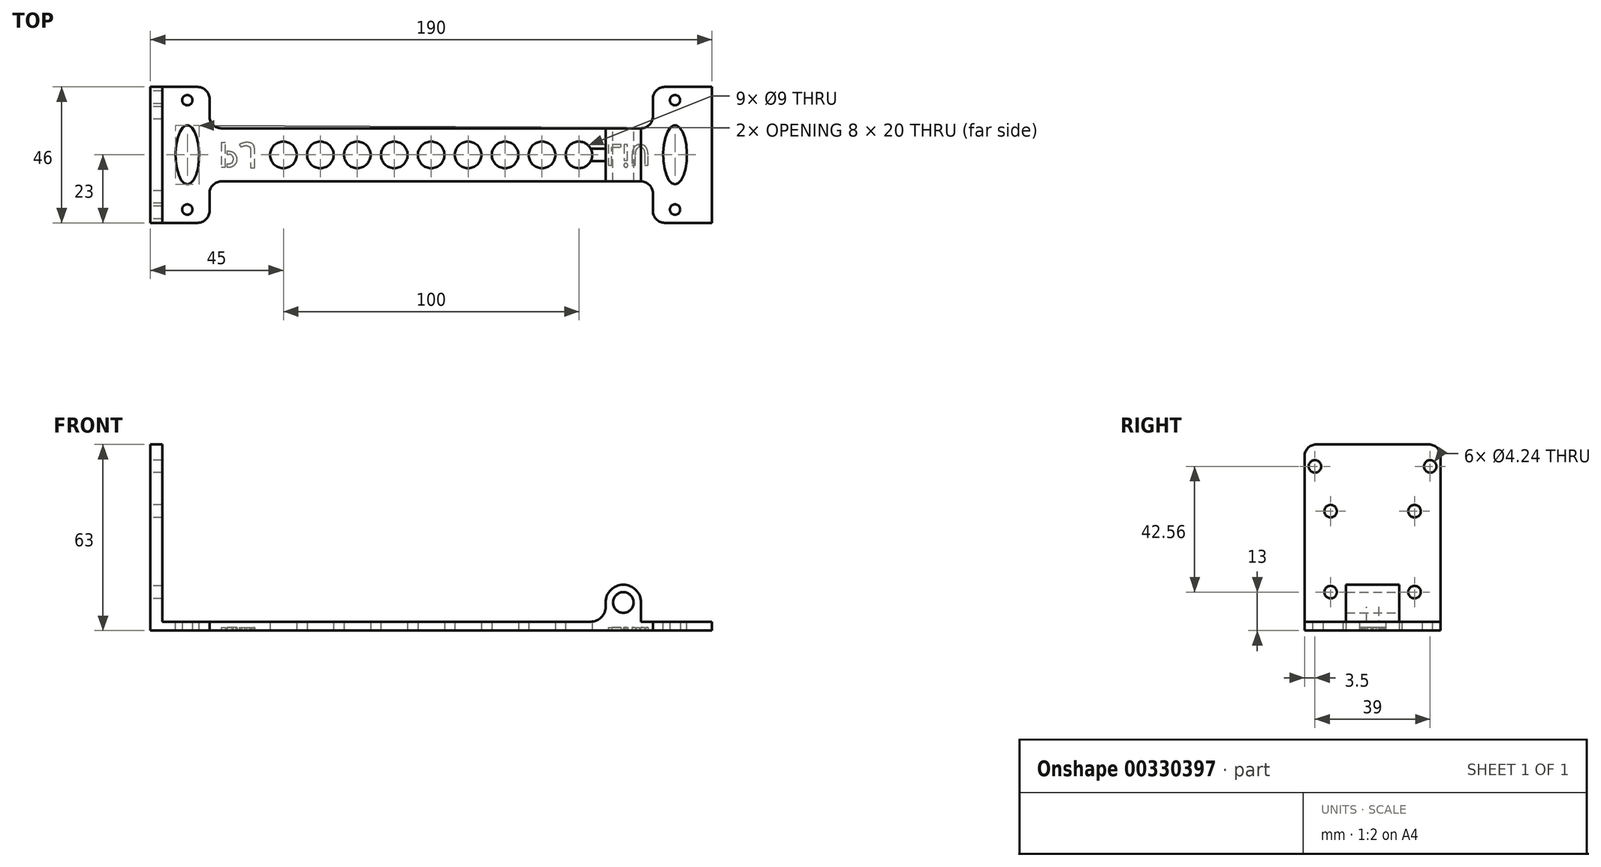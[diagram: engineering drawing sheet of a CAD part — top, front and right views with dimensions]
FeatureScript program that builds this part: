
annotation { "Feature Type Name" : "Feature", "Feature Type Description" : "" }
export const myFeature = defineFeature(function(context is Context, id is Id, definition is map)
    precondition{}
    {
        {
            var Q0;
            Q0=qCreatedBy(makeId("Top.planeOp"),FACE);
            var sketch = newSketch(context, id + "F0", { "sketchPlane" : qUnion([Q0])});
            skLineSegment(sketch, "E0.bottom", {"start": v(-75, 9) * mm, "end": v(75, 9) * mm});
            skLineSegment(sketch, "E0.top", {"start": v(-75, -9) * mm, "end": v(75, -9) * mm});
            skLineSegment(sketch, "E0.left", {"start": v(-75, 9) * mm, "end": v(-75, -9) * mm});
            skLineSegment(sketch, "E0.right", {"start": v(75, 9) * mm, "end": v(75, -9) * mm});
            skPoint(sketch, "E0.middle", {"position": v(0, 0) * mm});
            skLineSegment(sketch, "E1", {"start": v(-95, 23) * mm, "end": v(-95, -23) * mm});
            skPoint(sketch, "E2.middle.positionSnap0", {"position": v(0, 9) * mm});
            skPoint(sketch, "E2.centerSnap0", {"position": v(0, 9) * mm});
            skCircle(sketch, "E3", {"center": v(-82.5, 18.5) * mm, "radius": 1.75 * mm});
            skCircle(sketch, "E4.MirrorC", {"center": v(-82.5, -18.5) * mm, "radius": 1.75 * mm});
            skLineSegment(sketch, "E5", {"start": v(-95, 23) * mm, "end": v(-75, 23) * mm});
            skLineSegment(sketch, "E6", {"start": v(-75, 9) * mm, "end": v(-75, 23) * mm});
            skLineSegment(sketch, "E7.MirrorCS", {"start": v(-95, -23) * mm, "end": v(-75, -23) * mm});
            skLineSegment(sketch, "E8.MirrorCS", {"start": v(-75, -9) * mm, "end": v(-75, -23) * mm});
            skLineSegment(sketch, "E9.MirrorCS", {"start": v(95, 23) * mm, "end": v(95, -23) * mm});
            skLineSegment(sketch, "E10.MirrorCS", {"start": v(95, -23) * mm, "end": v(75, -23) * mm});
            skCircle(sketch, "E11.MirrorC", {"center": v(82.5, -18.5) * mm, "radius": 1.75 * mm});
            skCircle(sketch, "E12.MirrorC", {"center": v(82.5, 18.5) * mm, "radius": 1.75 * mm});
            skLineSegment(sketch, "E13.MirrorCS", {"start": v(95, 23) * mm, "end": v(75, 23) * mm});
            skLineSegment(sketch, "E14.MirrorCS", {"start": v(75, 9) * mm, "end": v(75, 23) * mm});
            skLineSegment(sketch, "E15.MirrorCS", {"start": v(75, -9) * mm, "end": v(75, -23) * mm});
            skSolve(sketch);
        }
        {
            var Q0;
            Q0=makeQuery(id+"F0.imprint","IMPRINT",FACE,{"disambiguationData":[TD([[makeQuery(id+"F0.imprint","IMPRINT",EDGE,{"derivedFrom":sQuery(id+"F0.wireOp",EDGE,"E0.bottom")}),-1.0]])]});
            var Q1;
            Q1=makeQuery(id+"F0.imprint","IMPRINT",FACE,{"disambiguationData":[TD([[makeQuery(id+"F0.imprint","IMPRINT",EDGE,{"derivedFrom":sQuery(id+"F0.wireOp",EDGE,"E0.left")}),-1.0]])]});
            var Q2;
            Q2=makeQuery(id+"F0.imprint","IMPRINT",FACE,{"disambiguationData":[TD([[makeQuery(id+"F0.imprint","IMPRINT",EDGE,{"derivedFrom":sQuery(id+"F0.wireOp",EDGE,"E0.right")}),1.0]])]});
            extrude(context, id + "F1", {"entities" : qUnion([Q0, Q1, Q2]), "endBound" : BoundingType.SYMMETRIC, "depth" : 3 * mm});
        }
        {
            var Q0;
            Q0=makeQuery(id+"F1.opExtrude","SWEPT_FACE",FACE,{"disambiguationData":[OSD([sQuery(id+"F0.wireOp",EDGE,"E0.bottom")])]});
            var sketch = newSketch(context, id + "F2", { "sketchPlane" : qUnion([Q0])});
            skCircle(sketch, "E16", {"center": v(-65, 8) * mm, "radius": 3.5 * mm});
            skArc(sketch, "E17", {"start": v(-59, 8) * mm, "mid": v(-65, 14) * mm, "end": v(-71, 8) * mm});
            skLineSegment(sketch, "E18", {"start": v(-59, 8) * mm, "end": v(-59, 1.5) * mm});
            skLineSegment(sketch, "E19", {"start": v(-71, 1.5) * mm, "end": v(-71, 8) * mm});
            skArc(sketch, "E20.MirrorCS", {"start": v(59, 8) * mm, "mid": v(65, 14) * mm, "end": v(71, 8) * mm});
            skLineSegment(sketch, "E21.MirrorCS", {"start": v(59, 8) * mm, "end": v(59, 1.5) * mm});
            skLineSegment(sketch, "E22.MirrorCS", {"start": v(71, 1.5) * mm, "end": v(71, 8) * mm});
            skCircle(sketch, "E23.MirrorC", {"center": v(65, 8) * mm, "radius": 3.5 * mm});
            skSolve(sketch);
        }
        {
            var Q0;
            Q0=makeQuery(id+"F2.imprint","IMPRINT",FACE,{"disambiguationData":[TD([[makeQuery(id+"F2.imprint","IMPRINT",EDGE,{"derivedFrom":sQuery(id+"F2.wireOp",EDGE,"E16")}),-1.0]])]});
            var Q1;
            Q1=makeQuery(id+"F2.imprint","IMPRINT",FACE,{"disambiguationData":[TD([[makeQuery(id+"F2.imprint","IMPRINT",EDGE,{"derivedFrom":sQuery(id+"F2.wireOp",EDGE,"E20.MirrorCS")}),-1.0]])]});
            extrude(context, id + "F3", {"entities" : qUnion([Q0, Q1]), "operationType" : NewBodyOperationType.ADD, "oppositeDirection" : true, "depth" : 18 * mm});
        }
        {
            var Q0;
            Q0=makeQuery(id+"F1.opExtrude","CAP_FACE",FACE,{"disambiguationData":[OSD([sQuery(id+"F0.wireOp",EDGE,"E0.bottom"),sQuery(id+"F0.wireOp",EDGE,"E0.top"),sQuery(id+"F0.wireOp",EDGE,"E1"),sQuery(id+"F0.wireOp",EDGE,"E3"),sQuery(id+"F0.wireOp",EDGE,"E4.MirrorC"),sQuery(id+"F0.wireOp",EDGE,"E5"),sQuery(id+"F0.wireOp",EDGE,"E6"),sQuery(id+"F0.wireOp",EDGE,"E7.MirrorCS"),sQuery(id+"F0.wireOp",EDGE,"E8.MirrorCS"),sQuery(id+"F0.wireOp",EDGE,"E9.MirrorCS"),sQuery(id+"F0.wireOp",EDGE,"E10.MirrorCS"),sQuery(id+"F0.wireOp",EDGE,"E11.MirrorC"),sQuery(id+"F0.wireOp",EDGE,"E12.MirrorC"),sQuery(id+"F0.wireOp",EDGE,"E13.MirrorCS"),sQuery(id+"F0.wireOp",EDGE,"E14.MirrorCS"),sQuery(id+"F0.wireOp",EDGE,"E15.MirrorCS")])],"isStart":true});
            var sketch = newSketch(context, id + "F4", { "sketchPlane" : qUnion([Q0])});
            skCircle(sketch, "E24", {"center": v(-50, 0) * mm, "radius": 4.5 * mm});
            skCircle(sketch, "E25.1.0.0", {"center": v(-37.5, 0) * mm, "radius": 4.5 * mm});
            skCircle(sketch, "E25.2.0.0", {"center": v(-25, 0) * mm, "radius": 4.5 * mm});
            skCircle(sketch, "E25.3.0.0", {"center": v(-12.5, 0) * mm, "radius": 4.5 * mm});
            skCircle(sketch, "E25.4.0.0", {"center": v(0, 0) * mm, "radius": 4.5 * mm});
            skCircle(sketch, "E25.5.0.0", {"center": v(12.5, 0) * mm, "radius": 4.5 * mm});
            skCircle(sketch, "E25.6.0.0", {"center": v(25, 0) * mm, "radius": 4.5 * mm});
            skCircle(sketch, "E25.7.0.0", {"center": v(37.5, 0) * mm, "radius": 4.5 * mm});
            skCircle(sketch, "E25.8.0.0", {"center": v(50, 0) * mm, "radius": 4.5 * mm});
            skLineSegment(sketch, "E25.direction1", {"start": v(-50, 0) * mm, "end": v(-37.5, 0) * mm, "construction": true});
            skEllipse(sketch, "E26", {"center": v(-82.5, 0) * mm, "majorRadius": 10 * mm, "minorRadius": 4 * mm, "majorAxis": v(0, 1)});
            skEllipse(sketch, "E27.MirrorC", {"center": v(82.5, 0) * mm, "majorRadius": 10 * mm, "minorRadius": 4 * mm, "majorAxis": v(0, 1)});
            skSolve(sketch);
        }
        {
            var Q0;
            Q0=makeQuery(id+"F4.imprint","IMPRINT",FACE,{"disambiguationData":[TD([[makeQuery(id+"F4.imprint","IMPRINT",EDGE,{"derivedFrom":sQuery(id+"F4.wireOp",EDGE,"E24")}),1.0]])]});
            var Q1;
            Q1=makeQuery(id+"F4.imprint","IMPRINT",FACE,{"disambiguationData":[TD([[makeQuery(id+"F4.imprint","IMPRINT",EDGE,{"derivedFrom":sQuery(id+"F4.wireOp",EDGE,"E25.1.0.0")}),1.0]])]});
            var Q2;
            Q2=makeQuery(id+"F4.imprint","IMPRINT",FACE,{"disambiguationData":[TD([[makeQuery(id+"F4.imprint","IMPRINT",EDGE,{"derivedFrom":sQuery(id+"F4.wireOp",EDGE,"E25.2.0.0")}),1.0]])]});
            var Q3;
            Q3=makeQuery(id+"F4.imprint","IMPRINT",FACE,{"disambiguationData":[TD([[makeQuery(id+"F4.imprint","IMPRINT",EDGE,{"derivedFrom":sQuery(id+"F4.wireOp",EDGE,"E25.3.0.0")}),1.0]])]});
            var Q4;
            Q4=makeQuery(id+"F4.imprint","IMPRINT",FACE,{"disambiguationData":[TD([[makeQuery(id+"F4.imprint","IMPRINT",EDGE,{"derivedFrom":sQuery(id+"F4.wireOp",EDGE,"E25.4.0.0")}),1.0]])]});
            var Q5;
            Q5=makeQuery(id+"F4.imprint","IMPRINT",FACE,{"disambiguationData":[TD([[makeQuery(id+"F4.imprint","IMPRINT",EDGE,{"derivedFrom":sQuery(id+"F4.wireOp",EDGE,"E25.5.0.0")}),1.0]])]});
            var Q6;
            Q6=makeQuery(id+"F4.imprint","IMPRINT",FACE,{"disambiguationData":[TD([[makeQuery(id+"F4.imprint","IMPRINT",EDGE,{"derivedFrom":sQuery(id+"F4.wireOp",EDGE,"E25.6.0.0")}),1.0]])]});
            var Q7;
            Q7=makeQuery(id+"F4.imprint","IMPRINT",FACE,{"disambiguationData":[TD([[makeQuery(id+"F4.imprint","IMPRINT",EDGE,{"derivedFrom":sQuery(id+"F4.wireOp",EDGE,"E25.7.0.0")}),1.0]])]});
            var Q8;
            Q8=makeQuery(id+"F4.imprint","IMPRINT",FACE,{"disambiguationData":[TD([[makeQuery(id+"F4.imprint","IMPRINT",EDGE,{"derivedFrom":sQuery(id+"F4.wireOp",EDGE,"E25.8.0.0")}),1.0]])]});
            var Q9;
            Q9=makeQuery(id+"F4.imprint","IMPRINT",FACE,{"disambiguationData":[TD([[makeQuery(id+"F4.imprint","IMPRINT",EDGE,{"derivedFrom":sQuery(id+"F4.wireOp",EDGE,"E26")}),1.0]])]});
            var Q10;
            Q10=makeQuery(id+"F4.imprint","IMPRINT",FACE,{"disambiguationData":[TD([[makeQuery(id+"F4.imprint","IMPRINT",EDGE,{"derivedFrom":sQuery(id+"F4.wireOp",EDGE,"E27.MirrorC")}),1.0]])]});
            extrude(context, id + "F5", {"entities" : qUnion([Q0, Q1, Q2, Q3, Q4, Q5, Q6, Q7, Q8, Q9, Q10]), "operationType" : NewBodyOperationType.REMOVE, "endBound" : BoundingType.UP_TO_NEXT, "oppositeDirection" : true, "depth" : 25 * mm});
        }
        {
            var Q0;
            Q0=makeQuery(id+"F3.opExtrude","SWEPT_EDGE",EDGE,{"disambiguationData":[OSD([sQuery(id+"F0.wireOp",EDGE,"E0.bottom"),sQuery(id+"F2.wireOp",EDGE,"E19")])]});
            var Q1;
            Q1=makeQuery(id+"F3.opExtrude","SWEPT_EDGE",EDGE,{"disambiguationData":[OSD([sQuery(id+"F0.wireOp",EDGE,"E0.bottom"),sQuery(id+"F2.wireOp",EDGE,"E18")])]});
            var Q2;
            Q2=makeQuery(id+"F3.opExtrude","SWEPT_EDGE",EDGE,{"disambiguationData":[OSD([sQuery(id+"F0.wireOp",EDGE,"E0.bottom"),sQuery(id+"F2.wireOp",EDGE,"E21.MirrorCS")])]});
            var Q3;
            Q3=makeQuery(id+"F3.opExtrude","SWEPT_EDGE",EDGE,{"disambiguationData":[OSD([sQuery(id+"F0.wireOp",EDGE,"E0.bottom"),sQuery(id+"F2.wireOp",EDGE,"E22.MirrorCS")])]});
            fillet(context, id + "F6", {"entities" : qUnion([Q0, Q1, Q2, Q3]), "radius" : 5 * mm, "tangentPropagation" : true, "allowEdgeOverflow" : false});
        }
        {
            var Q0;
            Q0=makeQuery(id+"F1.opExtrude","CAP_FACE",FACE,{"disambiguationData":[OSD([sQuery(id+"F0.wireOp",EDGE,"E0.bottom"),sQuery(id+"F0.wireOp",EDGE,"E0.top"),sQuery(id+"F0.wireOp",EDGE,"E1"),sQuery(id+"F0.wireOp",EDGE,"E3"),sQuery(id+"F0.wireOp",EDGE,"E4.MirrorC"),sQuery(id+"F0.wireOp",EDGE,"E5"),sQuery(id+"F0.wireOp",EDGE,"E6"),sQuery(id+"F0.wireOp",EDGE,"E7.MirrorCS"),sQuery(id+"F0.wireOp",EDGE,"E8.MirrorCS"),sQuery(id+"F0.wireOp",EDGE,"E9.MirrorCS"),sQuery(id+"F0.wireOp",EDGE,"E10.MirrorCS"),sQuery(id+"F0.wireOp",EDGE,"E11.MirrorC"),sQuery(id+"F0.wireOp",EDGE,"E12.MirrorC"),sQuery(id+"F0.wireOp",EDGE,"E13.MirrorCS"),sQuery(id+"F0.wireOp",EDGE,"E14.MirrorCS"),sQuery(id+"F0.wireOp",EDGE,"E15.MirrorCS")])],"isStart":true});
            var sketch = newSketch(context, id + "F7", { "sketchPlane" : qUnion([Q0])});
            skText(sketch, "E28", { "text": "PJ", "fontName": "AllertaStencil-Regular.ttf"});
            skText(sketch, "E29", { "text": "LiU", "fontName": "AllertaStencil-Regular.ttf"});
            const initialGuessF7  = {"E28": [-0.072, -0.00417, 1, 0, 0.00833], "E29": [0.059, -0.00346, 1, 0, 0.00692]};
            skSetInitialGuess(sketch, initialGuessF7);
            skSolve(sketch);
        }
        {
            var Q0;
            Q0=makeQuery(id+"F7.imprint","IMPRINT",FACE,{"disambiguationData":[TD([[makeQuery(id+"F7.imprint","IMPRINT",EDGE,{"derivedFrom":sQuery(id+"F7.wireOp",EDGE,"E28.sketch_text.stroke-4")}),-1.0]])]});
            var Q1;
            Q1=makeQuery(id+"F7.imprint","IMPRINT",FACE,{"disambiguationData":[TD([[makeQuery(id+"F7.imprint","IMPRINT",EDGE,{"derivedFrom":sQuery(id+"F7.wireOp",EDGE,"E28.sketch_text.stroke-0")}),-1.0]])]});
            var Q2;
            Q2=makeQuery(id+"F7.imprint","IMPRINT",FACE,{"disambiguationData":[TD([[makeQuery(id+"F7.imprint","IMPRINT",EDGE,{"derivedFrom":sQuery(id+"F7.wireOp",EDGE,"E28.sketch_text.stroke-26")}),-1.0]])]});
            var Q3;
            Q3=makeQuery(id+"F7.imprint","IMPRINT",FACE,{"disambiguationData":[TD([[makeQuery(id+"F7.imprint","IMPRINT",EDGE,{"derivedFrom":sQuery(id+"F7.wireOp",EDGE,"E29.sketch_text.stroke-0")}),-1.0]])]});
            var Q4;
            Q4=makeQuery(id+"F7.imprint","IMPRINT",FACE,{"disambiguationData":[TD([[makeQuery(id+"F7.imprint","IMPRINT",EDGE,{"derivedFrom":sQuery(id+"F7.wireOp",EDGE,"E29.sketch_text.stroke-6")}),-1.0]])]});
            var Q5;
            Q5=makeQuery(id+"F7.imprint","IMPRINT",FACE,{"disambiguationData":[TD([[makeQuery(id+"F7.imprint","IMPRINT",EDGE,{"derivedFrom":sQuery(id+"F7.wireOp",EDGE,"E29.sketch_text.stroke-10")}),-1.0]])]});
            var Q6;
            Q6=makeQuery(id+"F7.imprint","IMPRINT",FACE,{"disambiguationData":[TD([[makeQuery(id+"F7.imprint","IMPRINT",EDGE,{"derivedFrom":sQuery(id+"F7.wireOp",EDGE,"E29.sketch_text.stroke-18")}),-1.0]])]});
            var Q7;
            Q7=makeQuery(id+"F7.imprint","IMPRINT",FACE,{"disambiguationData":[TD([[makeQuery(id+"F7.imprint","IMPRINT",EDGE,{"derivedFrom":sQuery(id+"F7.wireOp",EDGE,"E29.sketch_text.stroke-30")}),-1.0]])]});
            extrude(context, id + "F8", {"entities" : qUnion([Q0, Q1, Q2, Q3, Q4, Q5, Q6, Q7]), "operationType" : NewBodyOperationType.REMOVE, "oppositeDirection" : true, "depth" : 1 * mm});
        }
        {
            var Q0;
            {var subQ4=sQuery(id+"F0.wireOp",EDGE,"E0.bottom");var subQ5=sQuery(id+"F0.wireOp",EDGE,"E3");var subQ6=sQuery(id+"F0.wireOp",EDGE,"E8.MirrorCS");var subQ7=sQuery(id+"F0.wireOp",EDGE,"E7.MirrorCS");var subQ8=sQuery(id+"F0.wireOp",EDGE,"E6");var subQ9=sQuery(id+"F0.wireOp",EDGE,"E5");var subQ10=sQuery(id+"F0.wireOp",EDGE,"E4.MirrorC");var subQ11=sQuery(id+"F0.wireOp",EDGE,"E0.top");var subQ12=sQuery(id+"F0.wireOp",EDGE,"E1");Q0=makeQuery(id+"F3.boolean.opBoolean","SPLIT",FACE,{"disambiguationData":[TD([makeQuery(id+"F1.opExtrude","SWEPT_FACE",FACE,{"disambiguationData":[OSD([subQ12])]})])],"derivedFrom":makeQuery(id+"F1.opExtrude","CAP_FACE",FACE,{"disambiguationData":[OSD([subQ4,subQ11,subQ12,subQ5,subQ10,subQ9,subQ8,subQ7,subQ6,sQuery(id+"F0.wireOp",EDGE,"E9.MirrorCS"),sQuery(id+"F0.wireOp",EDGE,"E10.MirrorCS"),sQuery(id+"F0.wireOp",EDGE,"E11.MirrorC"),sQuery(id+"F0.wireOp",EDGE,"E12.MirrorC"),sQuery(id+"F0.wireOp",EDGE,"E13.MirrorCS"),sQuery(id+"F0.wireOp",EDGE,"E14.MirrorCS"),sQuery(id+"F0.wireOp",EDGE,"E15.MirrorCS")])],"isStart":false})});}
            var sketch = newSketch(context, id + "F9", { "sketchPlane" : qUnion([Q0])});
            skLineSegment(sketch, "E30.bottom", {"start": v(-95, 23) * mm, "end": v(-91, 23) * mm});
            skLineSegment(sketch, "E30.top", {"start": v(-95, -23) * mm, "end": v(-91, -23) * mm});
            skLineSegment(sketch, "E30.left", {"start": v(-95, 23) * mm, "end": v(-95, -23) * mm});
            skLineSegment(sketch, "E30.right", {"start": v(-91, 23) * mm, "end": v(-91, -23) * mm});
            skLineSegment(sketch, "E31", {"start": v(0, 0) * mm, "end": v(0, 43.6) * mm, "construction": true});
            skSolve(sketch);
        }
        {
            var Q0;
            Q0=qSketchRegion(id+"F9",true);
            extrude(context, id + "F10", {"entities" : qUnion([Q0]), "operationType" : NewBodyOperationType.ADD, "depth" : 60 * mm});
        }
        {
            var Q0;
            Q0=makeQuery(id+"F10.boolean.opBoolean","MERGE",FACE,{"derivedFrom":[makeQuery(id+"F1.opExtrude","SWEPT_FACE",FACE,{"disambiguationData":[OSD([sQuery(id+"F0.wireOp",EDGE,"E1")])]}),makeQuery(id+"F10.opExtrude","SWEPT_FACE",FACE,{"disambiguationData":[OSD([sQuery(id+"F9.wireOp",EDGE,"E30.left")])]})]});
            var sketch = newSketch(context, id + "F11", { "sketchPlane" : qUnion([Q0])});
            skLineSegment(sketch, "E32", {"start": v(0, -7.58) * mm, "end": v(0, 34.79) * mm, "construction": true});
            skCircle(sketch, "E33", {"center": v(-14.2, 11.5) * mm, "radius": 2.12 * mm});
            skCircle(sketch, "E34.MirrorC", {"center": v(14.2, 11.5) * mm, "radius": 2.12 * mm});
            skLineSegment(sketch, "E35", {"start": v(-47.03, 25.2) * mm, "end": v(46.14, 25.2) * mm, "construction": true});
            skCircle(sketch, "E36.MirrorC", {"center": v(14.2, 38.9) * mm, "radius": 2.12 * mm});
            skCircle(sketch, "E37.MirrorC", {"center": v(-14.2, 38.9) * mm, "radius": 2.12 * mm});
            skLineSegment(sketch, "E38", {"start": v(0, -13.13) * mm, "end": v(0, 67.78) * mm, "construction": true});
            skPoint(sketch, "E38.endSnap0", {"position": v(0, 13.6) * mm});
            skCircle(sketch, "E39.MirrorC", {"center": v(-19.5, 54.06) * mm, "radius": 2.12 * mm});
            skCircle(sketch, "E40.MirrorC", {"center": v(19.5, 54.06) * mm, "radius": 2.12 * mm});
            skSolve(sketch);
        }
        {
            var Q0;
            Q0=makeQuery(id+"F1.opExtrude","SWEPT_EDGE",EDGE,{"disambiguationData":[OSD([sQuery(id+"F0.wireOp",EDGE,"E5"),sQuery(id+"F0.wireOp",EDGE,"E6")])]});
            var Q1;
            Q1=makeQuery(id+"F1.opExtrude","SWEPT_EDGE",EDGE,{"disambiguationData":[OSD([sQuery(id+"F0.wireOp",EDGE,"E7.MirrorCS"),sQuery(id+"F0.wireOp",EDGE,"E8.MirrorCS")])]});
            var Q2;
            Q2=makeQuery(id+"F1.opExtrude","SWEPT_EDGE",EDGE,{"disambiguationData":[OSD([sQuery(id+"F0.wireOp",EDGE,"E13.MirrorCS"),sQuery(id+"F0.wireOp",EDGE,"E14.MirrorCS")])]});
            var Q3;
            Q3=makeQuery(id+"F1.opExtrude","SWEPT_EDGE",EDGE,{"disambiguationData":[OSD([sQuery(id+"F0.wireOp",EDGE,"E10.MirrorCS"),sQuery(id+"F0.wireOp",EDGE,"E15.MirrorCS")])]});
            var Q4;
            Q4=makeQuery(id+"F1.opExtrude","SWEPT_EDGE",EDGE,{"disambiguationData":[OSD([sQuery(id+"F0.wireOp",EDGE,"E0.bottom"),sQuery(id+"F0.wireOp",EDGE,"E0.left"),sQuery(id+"F0.wireOp",EDGE,"E6")])]});
            var Q5;
            Q5=makeQuery(id+"F1.opExtrude","SWEPT_EDGE",EDGE,{"disambiguationData":[OSD([sQuery(id+"F0.wireOp",EDGE,"E0.top"),sQuery(id+"F0.wireOp",EDGE,"E0.left"),sQuery(id+"F0.wireOp",EDGE,"E8.MirrorCS")])]});
            var Q6;
            Q6=makeQuery(id+"F1.opExtrude","SWEPT_EDGE",EDGE,{"disambiguationData":[OSD([sQuery(id+"F0.wireOp",EDGE,"E0.top"),sQuery(id+"F0.wireOp",EDGE,"E0.right"),sQuery(id+"F0.wireOp",EDGE,"E15.MirrorCS")])]});
            var Q7;
            Q7=makeQuery(id+"F1.opExtrude","SWEPT_EDGE",EDGE,{"disambiguationData":[OSD([sQuery(id+"F0.wireOp",EDGE,"E0.bottom"),sQuery(id+"F0.wireOp",EDGE,"E0.right"),sQuery(id+"F0.wireOp",EDGE,"E14.MirrorCS")])]});
            var Q8;
            Q8=makeQuery(id+"F10.opExtrude","CAP_EDGE",EDGE,{"disambiguationData":[OSD([sQuery(id+"F9.wireOp",EDGE,"E30.top")])],"isStart":false});
            var Q9;
            Q9=makeQuery(id+"F10.opExtrude","CAP_EDGE",EDGE,{"disambiguationData":[OSD([sQuery(id+"F9.wireOp",EDGE,"E30.bottom")])],"isStart":false});
            var Q10;
            Q10=makeQuery(id+"F10.opExtrude","CAP_EDGE",EDGE,{"disambiguationData":[OSD([sQuery(id+"F9.wireOp",EDGE,"546b42b7-9f8a-4aab-89ce-59dfc89117bd0.MirrorCS")])],"isStart":false});
            var Q11;
            Q11=makeQuery(id+"F10.opExtrude","CAP_EDGE",EDGE,{"disambiguationData":[OSD([sQuery(id+"F9.wireOp",EDGE,"5addfbc6-1e7e-4302-a89f-a30cf9bc3fd90.MirrorCS")])],"isStart":false});
            fillet(context, id + "F12", {"entities" : qUnion([Q0, Q1, Q2, Q3, Q4, Q5, Q6, Q7, Q8, Q9, Q10, Q11]), "radius" : 4 * mm, "tangentPropagation" : true, "allowEdgeOverflow" : false});
        }
        {
            var Q0;
            Q0 = qSketchRegion(id + "F11", true);
            var Q1;
            Q1=makeQuery(id+"F10.opExtrude","SWEPT_FACE",FACE,{"disambiguationData":[OSD([sQuery(id+"F9.wireOp",EDGE,"E30.right")])]});
            extrude(context, id + "F13", {"entities" : qUnion([Q0]), "operationType" : NewBodyOperationType.REMOVE, "endBound" : BoundingType.UP_TO_SURFACE, "oppositeDirection" : true, "endBoundEntityFace" : qUnion([Q1]), "depth" : 25 * mm});
        }
    });
